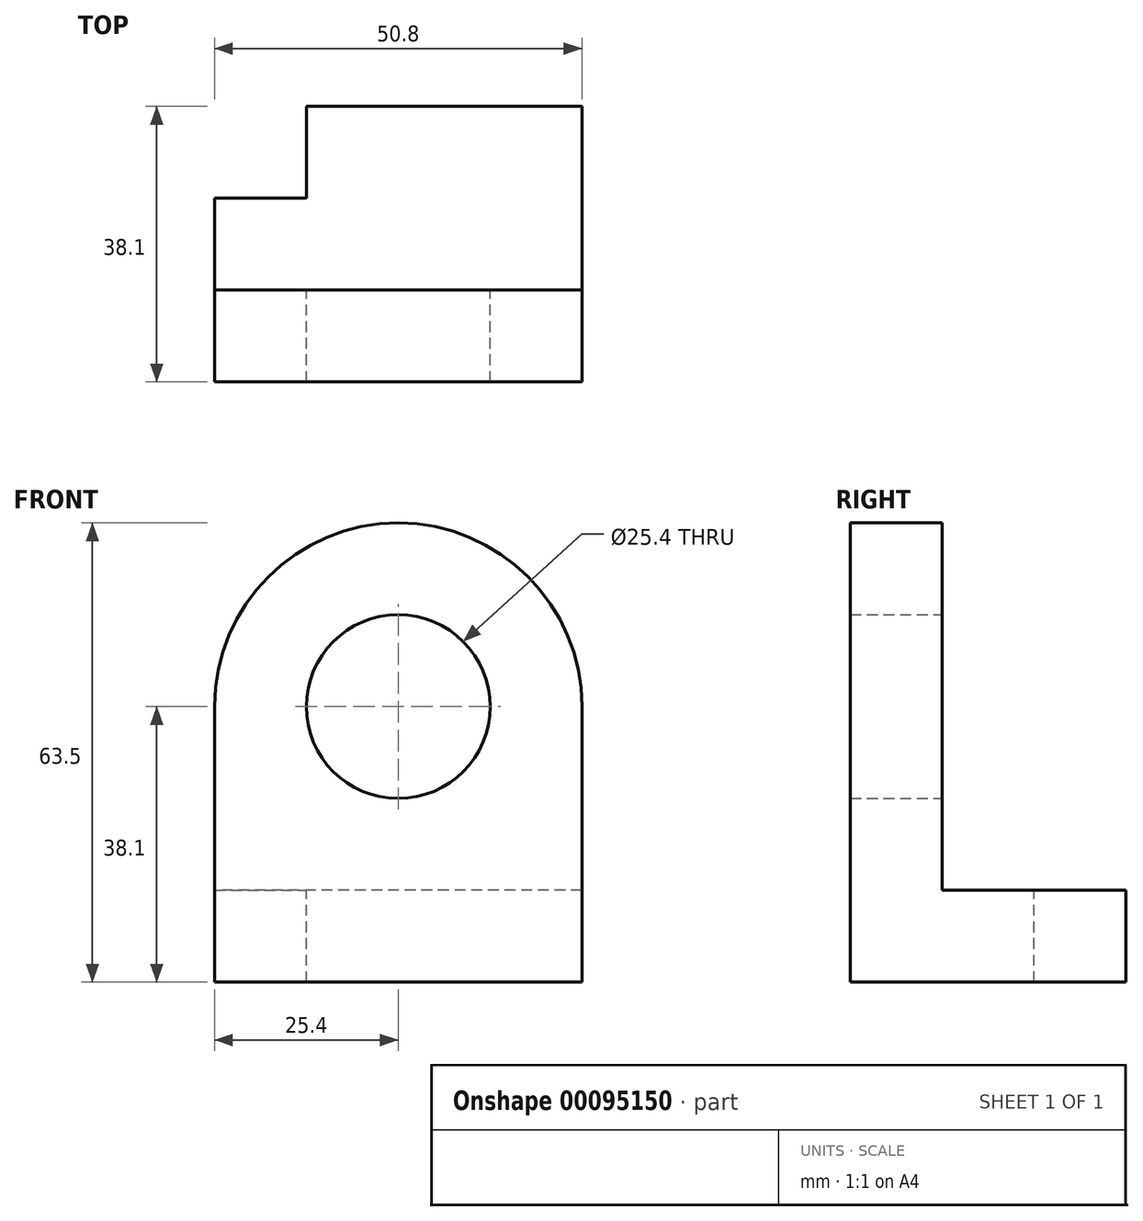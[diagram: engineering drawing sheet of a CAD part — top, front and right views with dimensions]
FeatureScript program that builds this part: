
annotation { "Feature Type Name" : "Feature", "Feature Type Description" : "" }
export const myFeature = defineFeature(function(context is Context, id is Id, definition is map)
    precondition{}
    {
        {
            var Q0;
            Q0=qCreatedBy(makeId("Top.planeOp"),FACE);
            var sketch = newSketch(context, id + "F0", { "sketchPlane" : qUnion([Q0])});
            skLineSegment(sketch, "E0.bottom", {"start": v(0, 38.1) * mm, "end": v(-50.8, 38.1) * mm});
            skLineSegment(sketch, "E0.top", {"start": v(0, 0) * mm, "end": v(-50.8, 0) * mm});
            skLineSegment(sketch, "E0.left", {"start": v(0, 38.1) * mm, "end": v(0, 0) * mm});
            skLineSegment(sketch, "E0.right", {"start": v(-50.8, 38.1) * mm, "end": v(-50.8, 0) * mm});
            skSolve(sketch);
        }
        {
            var Q0;
            Q0 = qSketchRegion(id + "F0", true);
            extrude(context, id + "F1", {"entities" : qUnion([Q0]), "depth" : 12.7 * mm});
        }
        {
            var Q0;
            Q0=makeQuery(id+"F1.opExtrude","CAP_FACE",FACE,{"disambiguationData":[OSD([sQuery(id+"F0.wireOp",EDGE,"E0.bottom"),sQuery(id+"F0.wireOp",EDGE,"E0.top"),sQuery(id+"F0.wireOp",EDGE,"E0.left"),sQuery(id+"F0.wireOp",EDGE,"E0.right")])],"isStart":true});
            var sketch = newSketch(context, id + "F2", { "sketchPlane" : qUnion([Q0])});
            skLineSegment(sketch, "E1.bottom", {"start": v(-50.8, 0) * mm, "end": v(0, 0) * mm});
            skLineSegment(sketch, "E1.top", {"start": v(-50.8, -12.7) * mm, "end": v(0, -12.7) * mm});
            skLineSegment(sketch, "E1.left", {"start": v(-50.8, -12.7) * mm, "end": v(-50.8, 0) * mm});
            skLineSegment(sketch, "E1.right", {"start": v(0, -12.7) * mm, "end": v(0, 0) * mm});
            skSolve(sketch);
        }
        {
            var Q0;
            Q0 = qSketchRegion(id + "F2", true);
            extrude(context, id + "F3", {"entities" : qUnion([Q0]), "operationType" : NewBodyOperationType.ADD, "oppositeDirection" : true, "depth" : 63.5 * mm});
        }
        {
            var Q0;
            Q0=makeQuery(id+"F1.opExtrude","CAP_FACE",FACE,{"disambiguationData":[OSD([sQuery(id+"F0.wireOp",EDGE,"E0.bottom"),sQuery(id+"F0.wireOp",EDGE,"E0.top"),sQuery(id+"F0.wireOp",EDGE,"E0.left"),sQuery(id+"F0.wireOp",EDGE,"E0.right")])],"isStart":false});
            var sketch = newSketch(context, id + "F4", { "sketchPlane" : qUnion([Q0])});
            skPoint(sketch, "E2.oppositeSnap0", {"position": v(-50.8, 25.4) * mm});
            skLineSegment(sketch, "E2.bottom", {"start": v(-50.8, 38.1) * mm, "end": v(-38.1, 38.1) * mm});
            skLineSegment(sketch, "E2.top", {"start": v(-50.8, 25.4) * mm, "end": v(-38.1, 25.4) * mm});
            skLineSegment(sketch, "E2.left", {"start": v(-50.8, 38.1) * mm, "end": v(-50.8, 25.4) * mm});
            skLineSegment(sketch, "E2.right", {"start": v(-38.1, 38.1) * mm, "end": v(-38.1, 25.4) * mm});
            skSolve(sketch);
        }
        {
            var Q0;
            Q0 = qSketchRegion(id + "F4", true);
            extrude(context, id + "F5", {"entities" : qUnion([Q0]), "operationType" : NewBodyOperationType.REMOVE, "endBound" : BoundingType.THROUGH_ALL, "oppositeDirection" : true, "depth" : 25.4 * mm});
        }
        {
            var Q0;
            Q0=makeQuery(id+"F3.opExtrude","SWEPT_FACE",FACE,{"disambiguationData":[OSD([sQuery(id+"F2.wireOp",EDGE,"E1.top")])]});
            var sketch = newSketch(context, id + "F6", { "sketchPlane" : qUnion([Q0])});
            skCircle(sketch, "E3", {"center": v(25.4, 38.1) * mm, "radius": 12.7 * mm});
            skSolve(sketch);
        }
        {
            var Q0;
            Q0 = qSketchRegion(id + "F6", true);
            extrude(context, id + "F7", {"entities" : qUnion([Q0]), "operationType" : NewBodyOperationType.REMOVE, "endBound" : BoundingType.THROUGH_ALL, "oppositeDirection" : true, "depth" : 25.4 * mm});
        }
        {
            var Q0;
            Q0=makeQuery(id+"F3.opExtrude","CAP_EDGE",EDGE,{"disambiguationData":[OSD([sQuery(id+"F2.wireOp",EDGE,"E1.left")])],"isStart":false});
            var Q1;
            Q1=makeQuery(id+"F3.opExtrude","CAP_EDGE",EDGE,{"disambiguationData":[OSD([sQuery(id+"F2.wireOp",EDGE,"E1.right")])],"isStart":false});
            fillet(context, id + "F8", {"entities" : qUnion([Q0, Q1]), "radius" : 25.4 * mm, "tangentPropagation" : true, "allowEdgeOverflow" : false});
        }
    });
